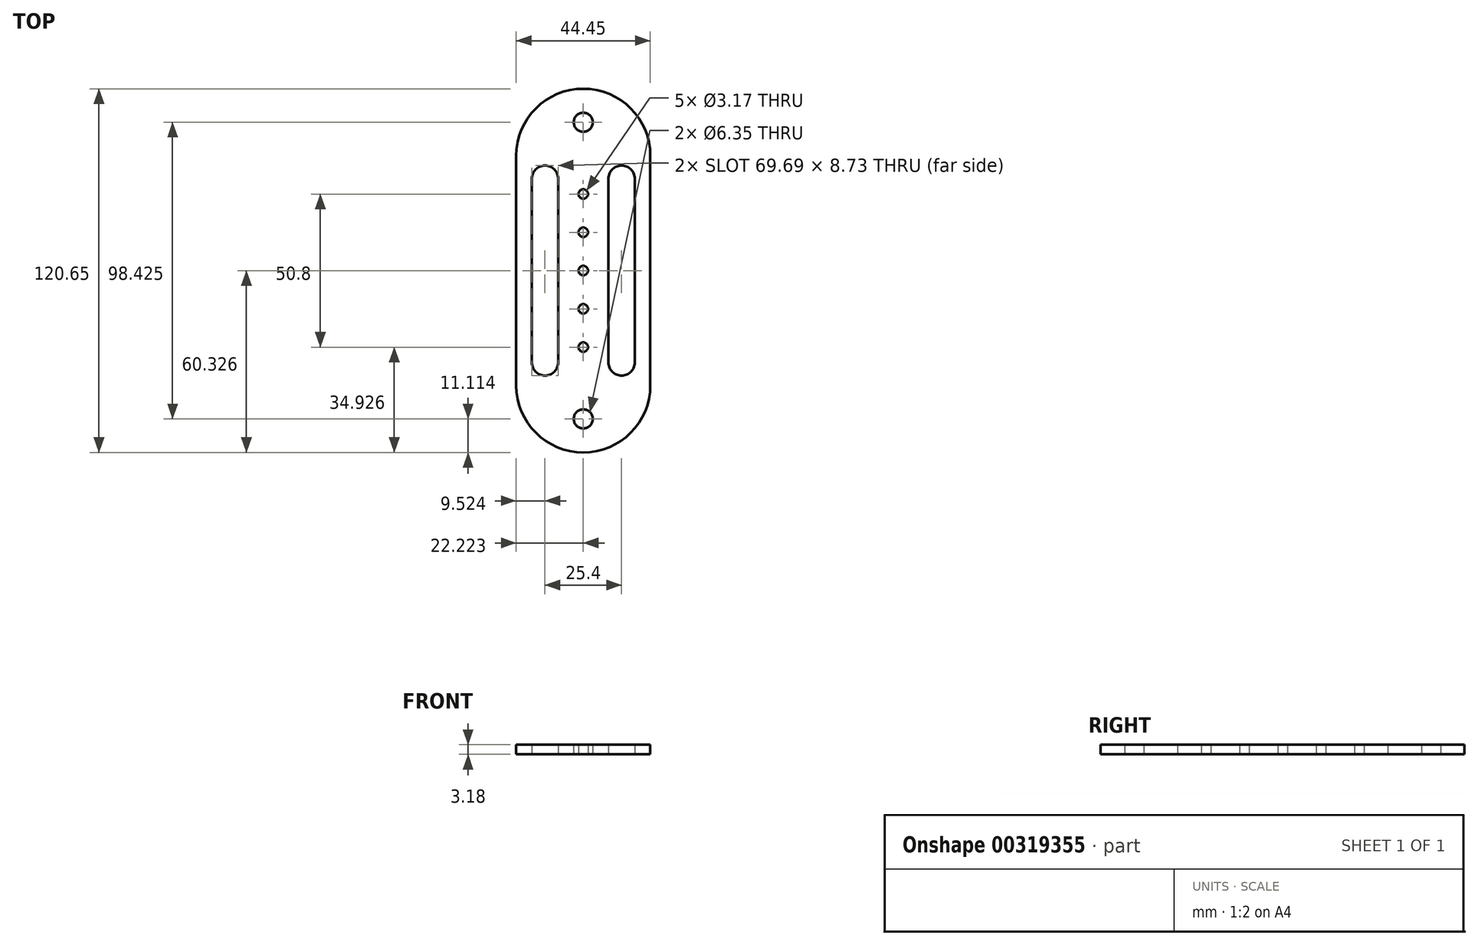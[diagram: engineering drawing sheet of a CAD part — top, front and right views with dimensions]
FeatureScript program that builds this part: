
annotation { "Feature Type Name" : "Feature", "Feature Type Description" : "" }
export const myFeature = defineFeature(function(context is Context, id is Id, definition is map)
    precondition{}
    {
        {
            var Q0;
            Q0=qCreatedBy(makeId("Top.planeOp"),FACE);
            var sketch = newSketch(context, id + "F0", { "sketchPlane" : qUnion([Q0])});
            skLineSegment(sketch, "E0.bottom", {"start": v(-27.72, 58.83) * mm, "end": v(16.73, 58.83) * mm});
            skLineSegment(sketch, "E0.top", {"start": v(-27.72, -17.37) * mm, "end": v(16.73, -17.37) * mm});
            skLineSegment(sketch, "E0.left", {"start": v(-27.72, 58.83) * mm, "end": v(-27.72, -17.37) * mm});
            skLineSegment(sketch, "E0.right", {"start": v(16.73, 58.83) * mm, "end": v(16.73, -17.37) * mm});
            skLineSegment(sketch, "E1", {"start": v(-27.72, 58.83) * mm, "end": v(-27.72, 51.2) * mm, "construction": true});
            skLineSegment(sketch, "E2", {"start": v(-27.72, 51.2) * mm, "end": v(-18.2, 51.2) * mm, "construction": true});
            skLineSegment(sketch, "E3", {"start": v(-18.2, 51.2) * mm, "end": v(7.2, 51.2) * mm, "construction": true});
            skLineSegment(sketch, "E4", {"start": v(7.2, 51.2) * mm, "end": v(16.73, 51.2) * mm, "construction": true});
            skArc(sketch, "E5", {"start": v(-22.56, 51.2) * mm, "mid": v(-18.2, 55.57) * mm, "end": v(-13.83, 51.2) * mm});
            skArc(sketch, "E6", {"start": v(2.84, 51.2) * mm, "mid": v(7.2, 55.57) * mm, "end": v(11.57, 51.2) * mm});
            skLineSegment(sketch, "E7", {"start": v(-27.72, -17.37) * mm, "end": v(-27.72, -9.75) * mm, "construction": true});
            skLineSegment(sketch, "E8", {"start": v(-27.72, -9.75) * mm, "end": v(-18.2, -9.75) * mm, "construction": true});
            skLineSegment(sketch, "E9", {"start": v(-18.2, -9.75) * mm, "end": v(7.2, -9.75) * mm, "construction": true});
            skLineSegment(sketch, "E10", {"start": v(7.2, -9.75) * mm, "end": v(16.73, -9.75) * mm, "construction": true});
            skArc(sketch, "E11", {"start": v(-22.56, -9.75) * mm, "mid": v(-18.2, -14.12) * mm, "end": v(-13.83, -9.75) * mm});
            skArc(sketch, "E12", {"start": v(2.84, -9.75) * mm, "mid": v(7.2, -14.12) * mm, "end": v(11.57, -9.75) * mm});
            skLineSegment(sketch, "E13", {"start": v(-22.56, -9.75) * mm, "end": v(-22.56, 51.2) * mm});
            skLineSegment(sketch, "E14", {"start": v(-13.83, 51.2) * mm, "end": v(-13.83, -9.75) * mm});
            skLineSegment(sketch, "E15", {"start": v(2.84, -9.75) * mm, "end": v(2.84, 51.2) * mm});
            skLineSegment(sketch, "E16", {"start": v(11.57, 51.2) * mm, "end": v(11.57, -9.75) * mm});
            skPoint(sketch, "E17", {"position": v(-5.5, 58.83) * mm});
            skPoint(sketch, "E18", {"position": v(-5.5, -17.37) * mm});
            skArc(sketch, "E19", {"start": v(16.73, -17.37) * mm, "mid": v(-5.5, -39.6) * mm, "end": v(-27.72, -17.37) * mm});
            skArc(sketch, "E20", {"start": v(16.73, 58.83) * mm, "mid": v(-5.5, 81.05) * mm, "end": v(-27.72, 58.83) * mm});
            skLineSegment(sketch, "E21", {"start": v(-5.5, 58.83) * mm, "end": v(-5.5, 81.05) * mm, "construction": true});
            skLineSegment(sketch, "E22", {"start": v(-5.5, -17.37) * mm, "end": v(-5.5, -39.6) * mm, "construction": true});
            skPoint(sketch, "E23", {"position": v(-5.5, -28.49) * mm});
            skPoint(sketch, "E24", {"position": v(-5.5, 69.94) * mm});
            skCircle(sketch, "E25", {"center": v(-5.5, 69.94) * mm, "radius": 3.18 * mm});
            skCircle(sketch, "E26", {"center": v(-5.5, -28.49) * mm, "radius": 3.18 * mm});
            skLineSegment(sketch, "E27", {"start": v(-5.5, -17.37) * mm, "end": v(-5.5, 58.83) * mm, "construction": true});
            skPoint(sketch, "E28", {"position": v(-5.5, 20.73) * mm});
            skCircle(sketch, "E29", {"center": v(-5.5, 20.73) * mm, "radius": 1.59 * mm});
            skLineSegment(sketch, "E30", {"start": v(-5.5, -17.37) * mm, "end": v(-5.5, -4.67) * mm, "construction": true});
            skLineSegment(sketch, "E31", {"start": v(-5.5, -4.67) * mm, "end": v(-5.5, 8.03) * mm, "construction": true});
            skLineSegment(sketch, "E32", {"start": v(-5.5, 8.03) * mm, "end": v(-5.5, 20.73) * mm, "construction": true});
            skLineSegment(sketch, "E33", {"start": v(-5.5, 20.73) * mm, "end": v(-5.5, 33.43) * mm, "construction": true});
            skLineSegment(sketch, "E34", {"start": v(-5.5, 33.43) * mm, "end": v(-5.5, 46.13) * mm, "construction": true});
            skLineSegment(sketch, "E35", {"start": v(-5.5, 46.13) * mm, "end": v(-5.5, 58.83) * mm, "construction": true});
            skCircle(sketch, "E36", {"center": v(-5.5, 8.03) * mm, "radius": 1.59 * mm});
            skCircle(sketch, "E37", {"center": v(-5.5, -4.67) * mm, "radius": 1.59 * mm});
            skCircle(sketch, "E38", {"center": v(-5.5, 33.43) * mm, "radius": 1.59 * mm});
            skCircle(sketch, "E39", {"center": v(-5.5, 46.13) * mm, "radius": 1.59 * mm});
            skSolve(sketch);
        }
        {
            var Q0;
            Q0 = qSketchRegion(id + "F0", true);
            extrude(context, id + "F1", {"entities" : qUnion([Q0]), "depth" : 3.17 * mm});
        }
    });
